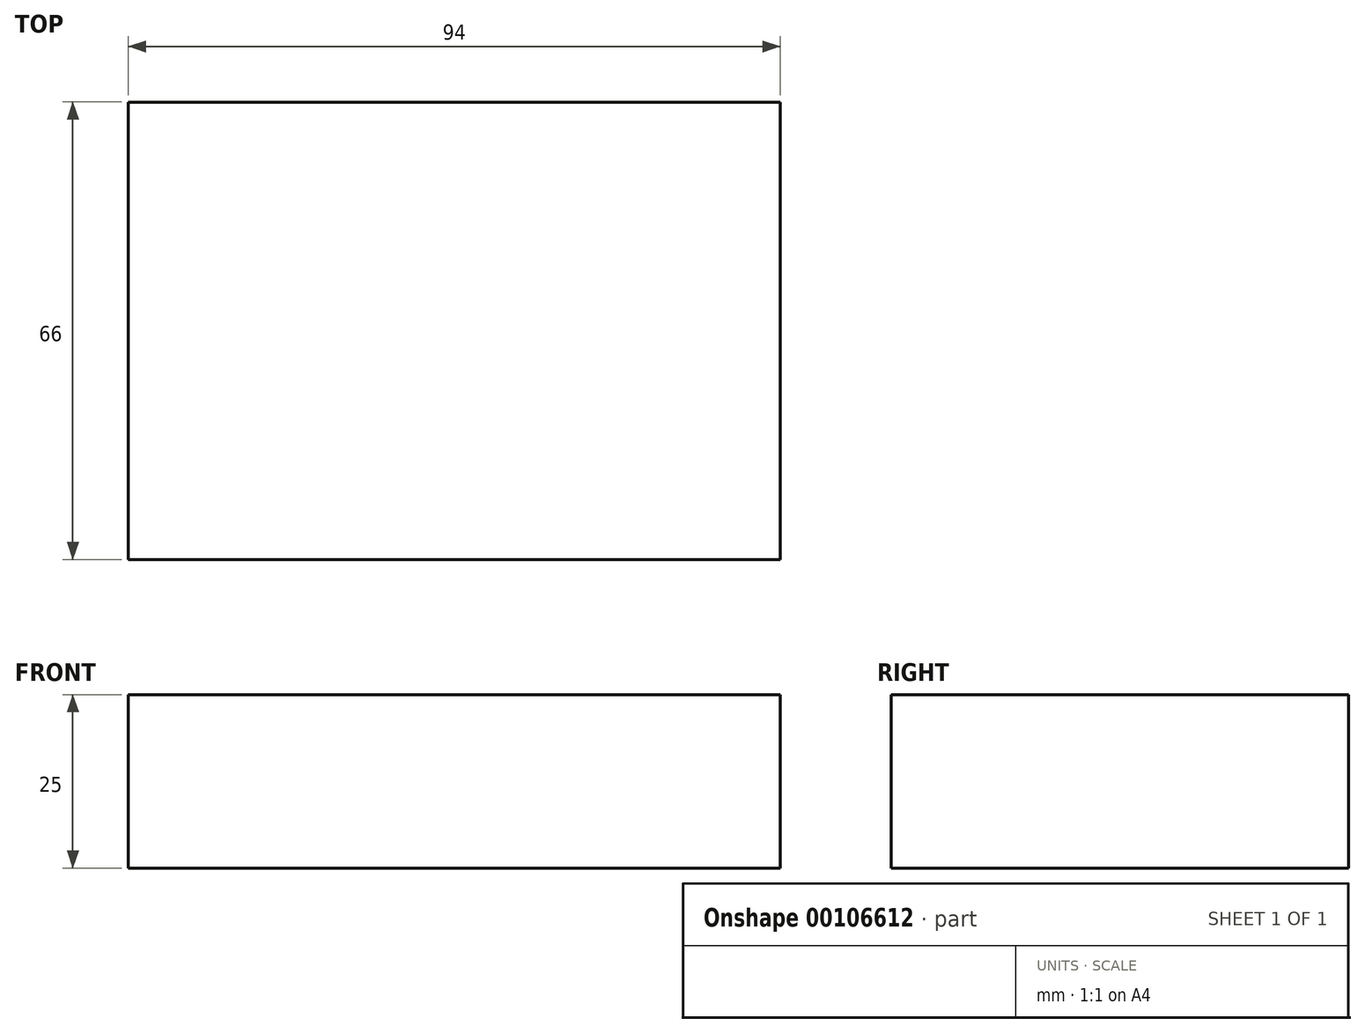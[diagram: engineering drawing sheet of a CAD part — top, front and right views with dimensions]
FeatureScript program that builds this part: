
annotation { "Feature Type Name" : "Feature", "Feature Type Description" : "" }
export const myFeature = defineFeature(function(context is Context, id is Id, definition is map)
    precondition{}
    {
        {
            var Q0;
            Q0=qCreatedBy(makeId("Top.planeOp"),FACE);
            var sketch = newSketch(context, id + "F0", { "sketchPlane" : qUnion([Q0])});
            skLineSegment(sketch, "E0.bottom", {"start": v(-75.62, 6.99) * mm, "end": v(18.38, 6.99) * mm});
            skLineSegment(sketch, "E0.top", {"start": v(-75.62, -59.01) * mm, "end": v(18.38, -59.01) * mm});
            skLineSegment(sketch, "E0.left", {"start": v(-75.62, 6.99) * mm, "end": v(-75.62, -59.01) * mm});
            skLineSegment(sketch, "E0.right", {"start": v(18.38, 6.99) * mm, "end": v(18.38, -59.01) * mm});
            skSolve(sketch);
        }
        {
            var Q0;
            Q0 = qSketchRegion(id + "F0", true);
            extrude(context, id + "F1", {"entities" : qUnion([Q0]), "depth" : 25 * mm});
        }
    });
